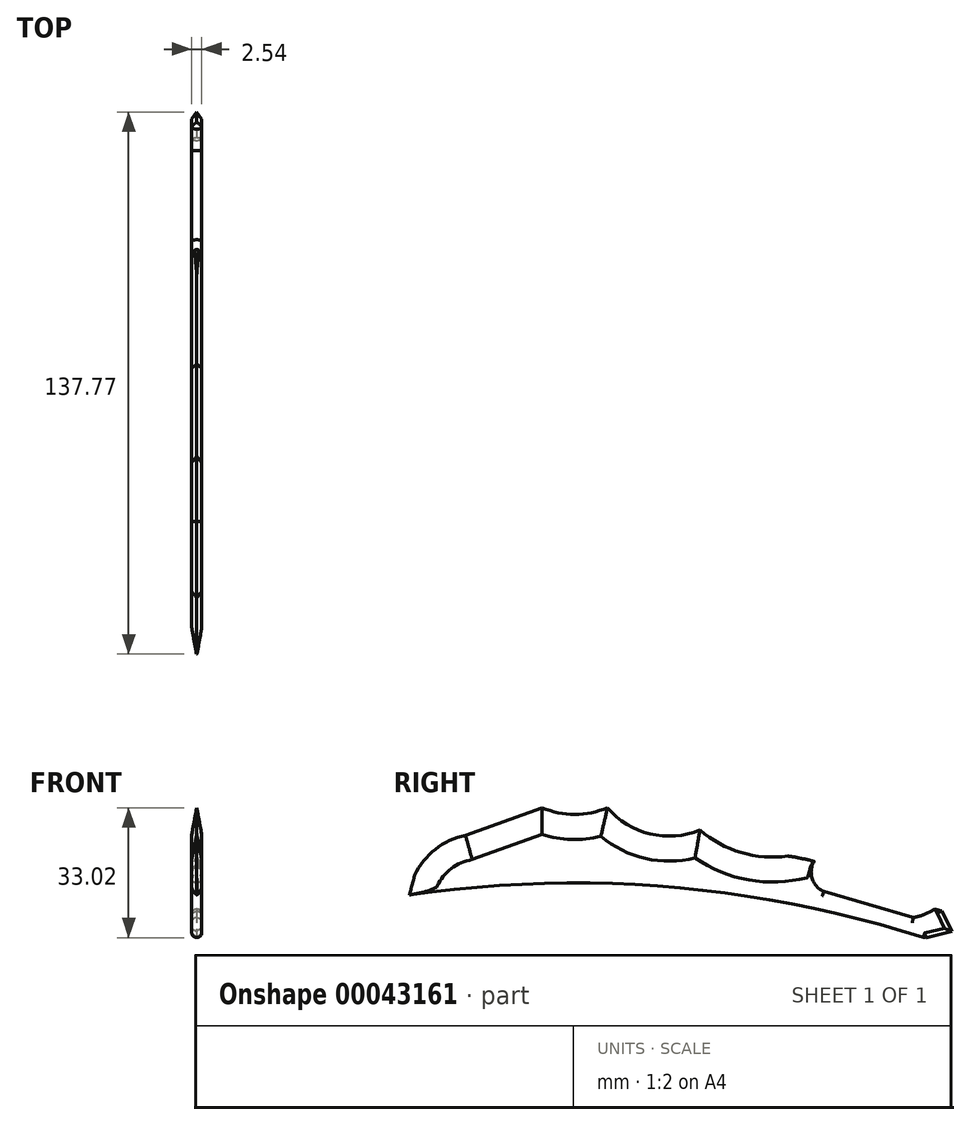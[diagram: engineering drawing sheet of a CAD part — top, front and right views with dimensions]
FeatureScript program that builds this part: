
annotation { "Feature Type Name" : "Feature", "Feature Type Description" : "" }
export const myFeature = defineFeature(function(context is Context, id is Id, definition is map)
    precondition{}
    {
        {
            var Q0;
            Q0=qCreatedBy(makeId("Right.planeOp"),FACE);
            var sketch = newSketch(context, id + "F0", { "sketchPlane" : qUnion([Q0])});
            skArc(sketch, "E0", {"start": v(57.08, -37.2) * mm, "mid": v(-7.72, -24.24) * mm, "end": v(-73.79, -26.27) * mm});
            skLineSegment(sketch, "E1", {"start": v(-59.53, -11.14) * mm, "end": v(-40.08, -4.1) * mm});
            skArc(sketch, "E2", {"start": v(-40.08, -4.1) * mm, "mid": v(-31.77, -5.83) * mm, "end": v(-23.45, -4.1) * mm});
            skArc(sketch, "E3", {"start": v(-23.45, -4.1) * mm, "mid": v(-12.65, -10.77) * mm, "end": v(0, -9.74) * mm});
            skArc(sketch, "E4", {"start": v(0, -9.74) * mm, "mid": v(10.47, -15.5) * mm, "end": v(22.4, -16.38) * mm});
            skLineSegment(sketch, "E5", {"start": v(-73.79, -26.27) * mm, "end": v(-72.45, -21.26) * mm});
            skArc(sketch, "E6", {"start": v(-59.53, -11.14) * mm, "mid": v(-67.19, -14.67) * mm, "end": v(-72.45, -21.26) * mm});
            skLineSegment(sketch, "E7", {"start": v(57.08, -37.2) * mm, "end": v(63.98, -35.59) * mm});
            skLineSegment(sketch, "E8", {"start": v(63.98, -35.59) * mm, "end": v(60.75, -28.95) * mm});
            skArc(sketch, "E9", {"start": v(54.12, -32.03) * mm, "mid": v(57.65, -30.95) * mm, "end": v(60.75, -28.95) * mm});
            skArc(sketch, "E10", {"start": v(29, -17.73) * mm, "mid": v(25.71, -16.98) * mm, "end": v(22.4, -16.38) * mm});
            skArc(sketch, "E11", {"start": v(29, -17.73) * mm, "mid": v(28.54, -22.12) * mm, "end": v(31.5, -25.4) * mm});
            skLineSegment(sketch, "E12", {"start": v(31.5, -25.4) * mm, "end": v(54.12, -32.03) * mm});
            skSolve(sketch);
        }
        {
            var Q0;
            Q0 = qSketchRegion(id + "F0", true);
            extrude(context, id + "F1", {"entities" : qUnion([Q0]), "endBound" : BoundingType.SYMMETRIC, "depth" : 2.54 * mm});
        }
        {
            var Q0;
            Q0=makeQuery(id+"F1.opExtrude","CAP_EDGE",EDGE,{"disambiguationData":[OSD([sQuery(id+"F0.wireOp",EDGE,"E12")])],"isStart":false});
            var Q1;
            Q1=makeQuery(id+"F1.opExtrude","CAP_EDGE",EDGE,{"disambiguationData":[OSD([sQuery(id+"F0.wireOp",EDGE,"E11")])],"isStart":true});
            var Q2;
            Q2=makeQuery(id+"F1.opExtrude","CAP_EDGE",EDGE,{"disambiguationData":[OSD([sQuery(id+"F0.wireOp",EDGE,"E12")])],"isStart":true});
            var Q3;
            Q3=makeQuery(id+"F1.opExtrude","CAP_EDGE",EDGE,{"disambiguationData":[OSD([sQuery(id+"F0.wireOp",EDGE,"E9")])],"isStart":false});
            var Q4;
            Q4=makeQuery(id+"F1.opExtrude","CAP_EDGE",EDGE,{"disambiguationData":[OSD([sQuery(id+"F0.wireOp",EDGE,"E9")])],"isStart":true});
            var Q5;
            Q5=makeQuery(id+"F1.opExtrude","CAP_EDGE",EDGE,{"disambiguationData":[OSD([sQuery(id+"F0.wireOp",EDGE,"E11")])],"isStart":false});
            var Q6;
            Q6=makeQuery(id+"F1.opExtrude","CAP_EDGE",EDGE,{"disambiguationData":[OSD([sQuery(id+"F0.wireOp",EDGE,"E0")])],"isStart":true});
            var Q7;
            Q7=makeQuery(id+"F1.opExtrude","CAP_EDGE",EDGE,{"disambiguationData":[OSD([sQuery(id+"F0.wireOp",EDGE,"E0")])],"isStart":false});
            fillet(context, id + "F2", {"entities" : qUnion([Q0, Q1, Q2, Q3, Q4, Q5, Q6, Q7]), "radius" : 1.27 * mm, "tangentPropagation" : true, "allowEdgeOverflow" : false});
        }
        {
            var Q0;
            Q0=makeQuery(id+"F1.opExtrude","CAP_EDGE",EDGE,{"disambiguationData":[OSD([sQuery(id+"F0.wireOp",EDGE,"E4")])],"isStart":true});
            var Q1;
            Q1=makeQuery(id+"F1.opExtrude","CAP_EDGE",EDGE,{"disambiguationData":[OSD([sQuery(id+"F0.wireOp",EDGE,"E3")])],"isStart":true});
            var Q2;
            Q2=makeQuery(id+"F1.opExtrude","CAP_EDGE",EDGE,{"disambiguationData":[OSD([sQuery(id+"F0.wireOp",EDGE,"E2")])],"isStart":true});
            var Q3;
            Q3=makeQuery(id+"F1.opExtrude","CAP_EDGE",EDGE,{"disambiguationData":[OSD([sQuery(id+"F0.wireOp",EDGE,"E1")])],"isStart":true});
            var Q4;
            Q4=makeQuery(id+"F1.opExtrude","CAP_EDGE",EDGE,{"disambiguationData":[OSD([sQuery(id+"F0.wireOp",EDGE,"E6")])],"isStart":true});
            chamfer(context, id + "F3", {"entities" : qUnion([Q0, Q1, Q2, Q3, Q4]), "chamferType" : ChamferType.TWO_OFFSETS, "width1" : 6.35 * mm, "oppositeDirection" : false, "width2" : 1.27 * mm, "tangentPropagation" : true});
        }
        {
            var Q0;
            Q0=makeQuery(id+"F1.opExtrude","CAP_EDGE",EDGE,{"disambiguationData":[OSD([sQuery(id+"F0.wireOp",EDGE,"E4")])],"isStart":false});
            var Q1;
            Q1=makeQuery(id+"F1.opExtrude","CAP_EDGE",EDGE,{"disambiguationData":[OSD([sQuery(id+"F0.wireOp",EDGE,"E3")])],"isStart":false});
            var Q2;
            Q2=makeQuery(id+"F1.opExtrude","CAP_EDGE",EDGE,{"disambiguationData":[OSD([sQuery(id+"F0.wireOp",EDGE,"E2")])],"isStart":false});
            var Q3;
            Q3=makeQuery(id+"F1.opExtrude","CAP_EDGE",EDGE,{"disambiguationData":[OSD([sQuery(id+"F0.wireOp",EDGE,"E1")])],"isStart":false});
            var Q4;
            Q4=makeQuery(id+"F1.opExtrude","CAP_EDGE",EDGE,{"disambiguationData":[OSD([sQuery(id+"F0.wireOp",EDGE,"E6")])],"isStart":false});
            chamfer(context, id + "F4", {"entities" : qUnion([Q0, Q1, Q2, Q3, Q4]), "chamferType" : ChamferType.TWO_OFFSETS, "width1" : 1.27 * mm, "oppositeDirection" : false, "width2" : 6.35 * mm, "tangentPropagation" : true});
        }
        {
            var Q0;
            Q0=makeQuery(id+"F1.opExtrude","CAP_EDGE",EDGE,{"disambiguationData":[OSD([sQuery(id+"F0.wireOp",EDGE,"E8")])],"isStart":false});
            var Q1;
            Q1=makeQuery(id+"F1.opExtrude","CAP_EDGE",EDGE,{"disambiguationData":[OSD([sQuery(id+"F0.wireOp",EDGE,"E7")])],"isStart":false});
            var Q2;
            Q2=makeQuery(id+"F1.opExtrude","CAP_EDGE",EDGE,{"disambiguationData":[OSD([sQuery(id+"F0.wireOp",EDGE,"E7")])],"isStart":true});
            chamfer(context, id + "F5", {"entities" : qUnion([Q0, Q1, Q2]), "chamferType" : ChamferType.TWO_OFFSETS, "width1" : 1.27 * mm, "oppositeDirection" : false, "width2" : 1.27 * mm, "tangentPropagation" : true});
        }
    });
